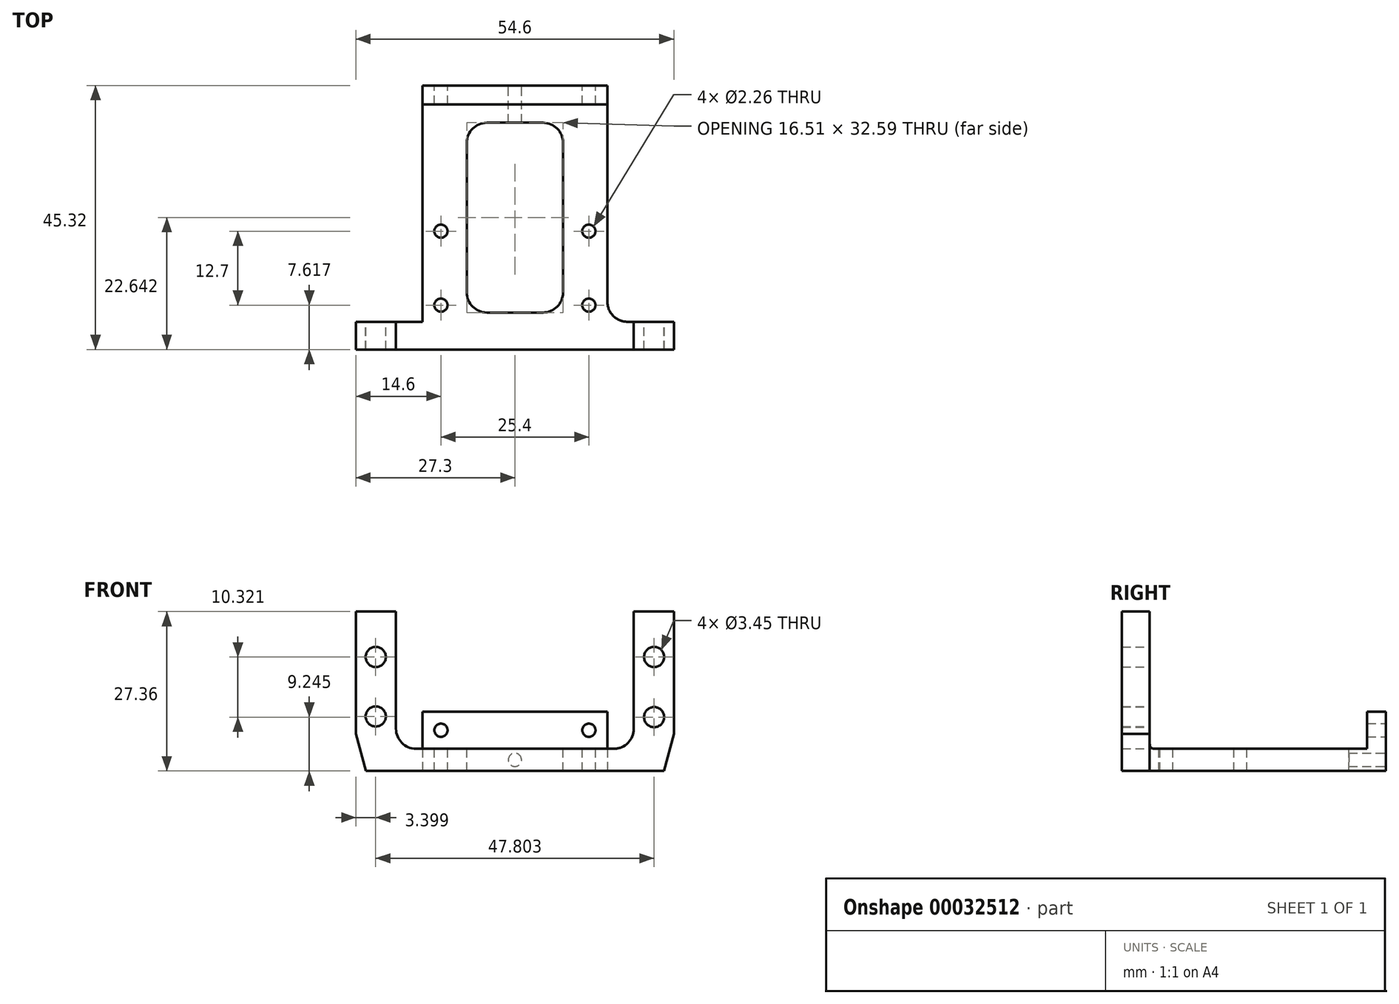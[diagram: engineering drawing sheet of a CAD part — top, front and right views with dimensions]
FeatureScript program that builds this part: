
annotation { "Feature Type Name" : "Feature", "Feature Type Description" : "" }
export const myFeature = defineFeature(function(context is Context, id is Id, definition is map)
    precondition{}
    {
        {
            var Q0;
            Q0=qCreatedBy(makeId("Front.planeOp"),FACE);
            var sketch = newSketch(context, id + "F0", { "sketchPlane" : qUnion([Q0])});
            skLineSegment(sketch, "E0.rect.bottom", {"start": v(0, -13.68) * mm, "end": v(-27.3, -13.68) * mm});
            skLineSegment(sketch, "E0.rect.right", {"start": v(-27.3, -7.33) * mm, "end": v(-27.3, 13.68) * mm});
            skPoint(sketch, "E0.rect.middle", {"position": v(0, 0) * mm});
            skLineSegment(sketch, "E1", {"start": v(0, -13.68) * mm, "end": v(0, 32.03) * mm, "construction": true});
            skPoint(sketch, "E1.endSnap0", {"position": v(0, 13.68) * mm});
            skLineSegment(sketch, "E2", {"start": v(-27.3, -13.68) * mm, "end": v(-55.76, -13.68) * mm, "construction": true});
            skLineSegment(sketch, "E3", {"start": v(-17, -9.87) * mm, "end": v(0, -9.87) * mm});
            skLineSegment(sketch, "E4", {"start": v(-20.42, 13.68) * mm, "end": v(-20.42, -6.44) * mm});
            skPoint(sketch, "E5.orphan", {"position": v(-27.3, -9.87) * mm});
            skPoint(sketch, "E6", {"position": v(-27.3, -7.33) * mm});
            skPoint(sketch, "E7", {"position": v(-25.6, -13.68) * mm});
            skLineSegment(sketch, "E8", {"start": v(-27.3, -7.33) * mm, "end": v(-25.6, -13.68) * mm});
            skLineSegment(sketch, "E9.trimOffspring", {"start": v(-20.42, 13.68) * mm, "end": v(-27.3, 13.68) * mm});
            skPoint(sketch, "E0.rect.left.end.orphan", {"position": v(27.3, 13.68) * mm});
            skPoint(sketch, "E10.orphan", {"position": v(27.3, -13.68) * mm});
            skLineSegment(sketch, "E11.MirrorCS", {"start": v(20.42, 13.68) * mm, "end": v(20.42, -6.44) * mm});
            skPoint(sketch, "E12.MirrorP", {"position": v(27.3, -9.87) * mm});
            skPoint(sketch, "E13.MirrorP", {"position": v(27.3, -7.33) * mm});
            skPoint(sketch, "E14.MirrorP", {"position": v(25.6, -13.68) * mm});
            skLineSegment(sketch, "E15.MirrorCS", {"start": v(27.3, -7.33) * mm, "end": v(25.6, -13.68) * mm});
            skLineSegment(sketch, "E16.MirrorCS", {"start": v(27.3, -7.33) * mm, "end": v(27.3, 13.68) * mm});
            skLineSegment(sketch, "E17.MirrorCS", {"start": v(20.42, 13.68) * mm, "end": v(27.3, 13.68) * mm});
            skLineSegment(sketch, "E18.MirrorCS", {"start": v(0, -13.68) * mm, "end": v(27.3, -13.68) * mm});
            skLineSegment(sketch, "E19.MirrorCS", {"start": v(17, -9.87) * mm, "end": v(0, -9.87) * mm});
            skPoint(sketch, "E20.visualSharp", {"position": v(-20.42, -9.87) * mm});
            skArc(sketch, "E20.filletArc", {"start": v(-20.42, -6.44) * mm, "mid": v(-19.42, -8.87) * mm, "end": v(-17, -9.87) * mm});
            skArc(sketch, "E21.MirrorCS", {"start": v(20.42, -6.44) * mm, "mid": v(19.42, -8.87) * mm, "end": v(17, -9.87) * mm});
            skPoint(sketch, "E22.orphan", {"position": v(20.42, -9.87) * mm});
            skSolve(sketch);
        }
        {
            var Q0;
            Q0=makeQuery(id+"F0.imprint","IMPRINT",FACE,{"disambiguationData":[TD([[makeQuery(id+"F0.imprint","IMPRINT",EDGE,{"derivedFrom":sQuery(id+"F0.wireOp",EDGE,"E0.rect.right")}),-1.0]])]});
            extrude(context, id + "F1", {"entities" : qUnion([Q0]), "depth" : 4.76 * mm});
        }
        {
            var Q0;
            Q0=makeQuery(id+"F1.opExtrude","CAP_FACE",FACE,{"disambiguationData":[OSD([sQuery(id+"F0.wireOp",EDGE,"E0.rect.bottom"),sQuery(id+"F0.wireOp",EDGE,"E0.rect.right"),sQuery(id+"F0.wireOp",EDGE,"E3"),sQuery(id+"F0.wireOp",EDGE,"E4"),sQuery(id+"F0.wireOp",EDGE,"E8"),sQuery(id+"F0.wireOp",EDGE,"E9.trimOffspring"),sQuery(id+"F0.wireOp",EDGE,"E11.MirrorCS"),sQuery(id+"F0.wireOp",EDGE,"E15.MirrorCS"),sQuery(id+"F0.wireOp",EDGE,"E16.MirrorCS"),sQuery(id+"F0.wireOp",EDGE,"E17.MirrorCS"),sQuery(id+"F0.wireOp",EDGE,"E18.MirrorCS"),sQuery(id+"F0.wireOp",EDGE,"E19.MirrorCS"),sQuery(id+"F0.wireOp",EDGE,"E20.filletArc"),sQuery(id+"F0.wireOp",EDGE,"E21.MirrorCS")])],"isStart":true});
            var sketch = newSketch(context, id + "F2", { "sketchPlane" : qUnion([Q0])});
            skLineSegment(sketch, "E23", {"start": v(0, -9.87) * mm, "end": v(-15.88, -9.87) * mm});
            skLineSegment(sketch, "E24", {"start": v(0, -9.87) * mm, "end": v(0, 6.26) * mm, "construction": true});
            skLineSegment(sketch, "E25", {"start": v(-24.83, -13.68) * mm, "end": v(-38.44, -13.68) * mm, "construction": true});
            skLineSegment(sketch, "E26", {"start": v(-15.88, -9.87) * mm, "end": v(-15.88, -13.68) * mm});
            skLineSegment(sketch, "E27", {"start": v(-15.88, -13.68) * mm, "end": v(0, -13.68) * mm});
            skLineSegment(sketch, "E28.MirrorCS", {"start": v(15.88, -9.87) * mm, "end": v(15.88, -13.68) * mm});
            skLineSegment(sketch, "E29.MirrorCS", {"start": v(15.88, -13.68) * mm, "end": v(0, -13.68) * mm});
            skLineSegment(sketch, "E30.MirrorCS", {"start": v(0, -9.87) * mm, "end": v(15.88, -9.87) * mm});
            skSolve(sketch);
        }
        {
            var Q0;
            Q0=makeQuery(id+"F2.imprint","IMPRINT",FACE,{"disambiguationData":[TD([[makeQuery(id+"F2.imprint","IMPRINT",EDGE,{"derivedFrom":sQuery(id+"F2.wireOp",EDGE,"E23")}),-1.0]])]});
            extrude(context, id + "F3", {"entities" : qUnion([Q0]), "operationType" : NewBodyOperationType.ADD, "depth" : 37.34 * mm});
        }
        {
            var Q0;
            Q0=makeQuery(id+"F3.opExtrude","CAP_EDGE",EDGE,{"disambiguationData":[OSD([sQuery(id+"F2.wireOp",EDGE,"E26")])],"isStart":true});
            var Q1;
            Q1=makeQuery(id+"F3.opExtrude","CAP_EDGE",EDGE,{"disambiguationData":[OSD([sQuery(id+"F2.wireOp",EDGE,"E28.MirrorCS")])],"isStart":true});
            fillet(context, id + "F4", {"entities" : qUnion([Q0, Q1]), "radius" : 3.43 * mm, "tangentPropagation" : true, "allowEdgeOverflow" : false});
        }
        {
            var Q0;
            Q0=makeQuery(id+"F3.opExtrude","CAP_FACE",FACE,{"disambiguationData":[OSD([sQuery(id+"F2.wireOp",EDGE,"E23"),sQuery(id+"F2.wireOp",EDGE,"E26"),sQuery(id+"F2.wireOp",EDGE,"E27"),sQuery(id+"F2.wireOp",EDGE,"E28.MirrorCS"),sQuery(id+"F2.wireOp",EDGE,"E29.MirrorCS"),sQuery(id+"F2.wireOp",EDGE,"E30.MirrorCS")])],"isStart":false});
            var sketch = newSketch(context, id + "F5", { "sketchPlane" : qUnion([Q0])});
            skLineSegment(sketch, "E31", {"start": v(-15.88, -13.68) * mm, "end": v(-15.88, -3.52) * mm});
            skLineSegment(sketch, "E32", {"start": v(15.88, -13.68) * mm, "end": v(15.88, -3.52) * mm});
            skPoint(sketch, "E32.endSnap0", {"position": v(15.88, -11.78) * mm});
            skLineSegment(sketch, "E33", {"start": v(-15.88, -3.52) * mm, "end": v(15.88, -3.52) * mm});
            skLineSegment(sketch, "E34", {"start": v(15.88, -13.68) * mm, "end": v(-15.88, -13.68) * mm});
            skSolve(sketch);
        }
        {
            var Q0;
            {var subQ1=sQuery(id+"F5.wireOp",EDGE,"E33");Q0=makeQuery(id+"F5.imprint","IMPRINT",FACE,{"disambiguationData":[TD([[makeQuery(id+"F5.imprint","IMPRINT",EDGE,{"derivedFrom":subQ1}),-1.0]])]});}
            var Q1;
            {var subQ1=sQuery(id+"F5.wireOp",EDGE,"E34");Q1=makeQuery(id+"F5.imprint","IMPRINT",FACE,{"disambiguationData":[TD([[makeQuery(id+"F5.imprint","IMPRINT",EDGE,{"derivedFrom":subQ1}),1.0]])]});}
            extrude(context, id + "F6", {"entities" : qUnion([Q0, Q1]), "operationType" : NewBodyOperationType.ADD, "depth" : 3.23 * mm});
        }
        {
            var Q0;
            Q0=qCreatedBy(makeId("Front.planeOp"),FACE);
            var sketch = newSketch(context, id + "F7", { "sketchPlane" : qUnion([Q0])});
            skLineSegment(sketch, "E35", {"start": v(0, -13.57) * mm, "end": v(0, 16.2) * mm, "construction": true});
            skLineSegment(sketch, "E36", {"start": v(0, -13.57) * mm, "end": v(-38.93, -13.57) * mm, "construction": true});
            skPoint(sketch, "E37", {"position": v(-23.9, -4.32) * mm});
            skPoint(sketch, "E38", {"position": v(-23.9, 5.89) * mm});
            skPoint(sketch, "E39", {"position": v(23.9, 5.89) * mm});
            skPoint(sketch, "E40", {"position": v(23.9, -4.43) * mm});
            skSolve(sketch);
        }
        {
            var Q0;
            Q0=sQuery(id+"F7.wireOp",VERTEX,"E38");
            var Q1;
            Q1=sQuery(id+"F7.wireOp",VERTEX,"E37");
            var Q2;
            Q2=sQuery(id+"F7.wireOp",VERTEX,"E40");
            var Q3;
            Q3=sQuery(id+"F7.wireOp",VERTEX,"E39");
            var Q4;
            Q4=makeQuery(id+"F1.opExtrude","SWEPT_BODY",BODY,{"disambiguationData":[OSD([sQuery(id+"F0.wireOp",EDGE,"E0.rect.bottom"),sQuery(id+"F0.wireOp",EDGE,"E0.rect.right"),sQuery(id+"F0.wireOp",EDGE,"E3"),sQuery(id+"F0.wireOp",EDGE,"E4"),sQuery(id+"F0.wireOp",EDGE,"E8"),sQuery(id+"F0.wireOp",EDGE,"E9.trimOffspring"),sQuery(id+"F0.wireOp",EDGE,"E11.MirrorCS"),sQuery(id+"F0.wireOp",EDGE,"E15.MirrorCS"),sQuery(id+"F0.wireOp",EDGE,"E16.MirrorCS"),sQuery(id+"F0.wireOp",EDGE,"E17.MirrorCS"),sQuery(id+"F0.wireOp",EDGE,"E18.MirrorCS"),sQuery(id+"F0.wireOp",EDGE,"E19.MirrorCS"),sQuery(id+"F0.wireOp",EDGE,"E20.filletArc"),sQuery(id+"F0.wireOp",EDGE,"E21.MirrorCS")])]});
            hole(context, id + "F8", {"style" : HoleStyle.SIMPLE, "holeDiameter" : 3.45 * mm, "endStyle" : HoleEndStyle.THROUGH, "oppositeDirection" : true, "locations" : qUnion([Q0, Q1, Q2, Q3]), "scope" : qUnion([Q4])});
        }
        {
            var Q0;
            Q0=makeQuery(id+"F6.opExtrude","CAP_FACE",FACE,{"disambiguationData":[OSD([sQuery(id+"F5.wireOp",EDGE,"E31"),sQuery(id+"F5.wireOp",EDGE,"E32"),sQuery(id+"F5.wireOp",EDGE,"E33"),sQuery(id+"F5.wireOp",EDGE,"E34")])],"isStart":false});
            var sketch = newSketch(context, id + "F9", { "sketchPlane" : qUnion([Q0])});
            skLineSegment(sketch, "E41", {"start": v(-15.88, -6.7) * mm, "end": v(15.88, -6.7) * mm});
            skLineSegment(sketch, "E42", {"start": v(0, -13.68) * mm, "end": v(0, 9.84) * mm, "construction": true});
            skPoint(sketch, "E42.endSnap0", {"position": v(0, -6.7) * mm});
            skLineSegment(sketch, "E43", {"start": v(0, -13.68) * mm, "end": v(-37.44, -13.68) * mm, "construction": true});
            skPoint(sketch, "E44", {"position": v(-12.7, -6.7) * mm});
            skPoint(sketch, "E45", {"position": v(12.7, -6.7) * mm});
            skPoint(sketch, "E46", {"position": v(0, -11.78) * mm});
            skSolve(sketch);
        }
        {
            var Q0;
            Q0=sQuery(id+"F9.wireOp",VERTEX,"E44");
            var Q1;
            Q1=sQuery(id+"F9.wireOp",VERTEX,"E45");
            var Q2;
            Q2=sQuery(id+"F9.wireOp",VERTEX,"E46");
            var Q3;
            Q3=makeQuery(id+"F1.opExtrude","SWEPT_BODY",BODY,{"disambiguationData":[OSD([sQuery(id+"F0.wireOp",EDGE,"E0.rect.bottom"),sQuery(id+"F0.wireOp",EDGE,"E0.rect.right"),sQuery(id+"F0.wireOp",EDGE,"E3"),sQuery(id+"F0.wireOp",EDGE,"E4"),sQuery(id+"F0.wireOp",EDGE,"E8"),sQuery(id+"F0.wireOp",EDGE,"E9.trimOffspring"),sQuery(id+"F0.wireOp",EDGE,"E11.MirrorCS"),sQuery(id+"F0.wireOp",EDGE,"E15.MirrorCS"),sQuery(id+"F0.wireOp",EDGE,"E16.MirrorCS"),sQuery(id+"F0.wireOp",EDGE,"E17.MirrorCS"),sQuery(id+"F0.wireOp",EDGE,"E18.MirrorCS"),sQuery(id+"F0.wireOp",EDGE,"E19.MirrorCS"),sQuery(id+"F0.wireOp",EDGE,"E20.filletArc"),sQuery(id+"F0.wireOp",EDGE,"E21.MirrorCS")])]});
            hole(context, id + "F10", {"style" : HoleStyle.SIMPLE, "holeDiameter" : 2.26 * mm, "endStyle" : HoleEndStyle.BLIND, "holeDepth" : 10.16 * mm, "locations" : qUnion([Q0, Q1, Q2]), "scope" : qUnion([Q3])});
        }
        {
            var Q0;
            Q0=makeQuery(id+"F3.boolean.opBoolean","MERGE",FACE,{"derivedFrom":[makeQuery(id+"F1.opExtrude","SWEPT_FACE",FACE,{"disambiguationData":[OSD([sQuery(id+"F0.wireOp",EDGE,"E3"),sQuery(id+"F0.wireOp",EDGE,"E19.MirrorCS")])]}),makeQuery(id+"F3.opExtrude","SWEPT_FACE",FACE,{"disambiguationData":[OSD([sQuery(id+"F2.wireOp",EDGE,"E23"),sQuery(id+"F2.wireOp",EDGE,"E30.MirrorCS")])]})]});
            var sketch = newSketch(context, id + "F11", { "sketchPlane" : qUnion([Q0])});
            skLineSegment(sketch, "E47.bottom", {"start": v(4.83, 1.59) * mm, "end": v(-4.83, 1.59) * mm});
            skLineSegment(sketch, "E47.top", {"start": v(4.83, 34.18) * mm, "end": v(-4.83, 34.18) * mm});
            skLineSegment(sketch, "E47.left", {"start": v(8.26, 5.02) * mm, "end": v(8.26, 30.75) * mm});
            skLineSegment(sketch, "E47.right", {"start": v(-8.26, 5.02) * mm, "end": v(-8.26, 30.75) * mm});
            skLineSegment(sketch, "E48", {"start": v(0, 0) * mm, "end": v(0, 47.79) * mm, "construction": true});
            skLineSegment(sketch, "E49", {"start": v(0, -4.76) * mm, "end": v(-43.2, -4.76) * mm, "construction": true});
            skPoint(sketch, "E50.visualSharp", {"position": v(8.26, 1.59) * mm});
            skArc(sketch, "E50.filletArc", {"start": v(4.83, 1.59) * mm, "mid": v(7.25, 2.6) * mm, "end": v(8.26, 5.02) * mm});
            skPoint(sketch, "E51.visualSharp", {"position": v(-8.26, 1.59) * mm});
            skArc(sketch, "E51.filletArc", {"start": v(-8.26, 5.02) * mm, "mid": v(-7.25, 2.6) * mm, "end": v(-4.83, 1.59) * mm});
            skPoint(sketch, "E52.visualSharp", {"position": v(-8.26, 34.18) * mm});
            skArc(sketch, "E52.filletArc", {"start": v(-4.83, 34.18) * mm, "mid": v(-7.25, 33.17) * mm, "end": v(-8.26, 30.75) * mm});
            skPoint(sketch, "E53.visualSharp", {"position": v(8.26, 34.18) * mm});
            skArc(sketch, "E53.filletArc", {"start": v(8.26, 30.75) * mm, "mid": v(7.25, 33.17) * mm, "end": v(4.83, 34.18) * mm});
            skSolve(sketch);
        }
        {
            var Q0;
            Q0=makeQuery(id+"F11.imprint","IMPRINT",FACE,{"disambiguationData":[TD([[makeQuery(id+"F11.imprint","IMPRINT",EDGE,{"derivedFrom":sQuery(id+"F11.wireOp",EDGE,"E47.bottom")}),-1.0]])]});
            extrude(context, id + "F12", {"entities" : qUnion([Q0]), "operationType" : NewBodyOperationType.REMOVE, "endBound" : BoundingType.THROUGH_ALL, "oppositeDirection" : true, "depth" : 25.4 * mm});
        }
        {
            var Q0;
            Q0=makeQuery(id+"F3.boolean.opBoolean","MERGE",FACE,{"derivedFrom":[makeQuery(id+"F1.opExtrude","SWEPT_FACE",FACE,{"disambiguationData":[OSD([sQuery(id+"F0.wireOp",EDGE,"E3"),sQuery(id+"F0.wireOp",EDGE,"E19.MirrorCS")])]}),makeQuery(id+"F3.opExtrude","SWEPT_FACE",FACE,{"disambiguationData":[OSD([sQuery(id+"F2.wireOp",EDGE,"E23"),sQuery(id+"F2.wireOp",EDGE,"E30.MirrorCS")])]})]});
            var sketch = newSketch(context, id + "F13", { "sketchPlane" : qUnion([Q0])});
            skLineSegment(sketch, "E54", {"start": v(0, -4.76) * mm, "end": v(0, 32.22) * mm, "construction": true});
            skLineSegment(sketch, "E55", {"start": v(-9.11, -4.76) * mm, "end": v(-39.22, -4.76) * mm, "construction": true});
            skPoint(sketch, "E56", {"position": v(12.7, 2.86) * mm});
            skPoint(sketch, "E57", {"position": v(12.7, 15.56) * mm});
            skPoint(sketch, "E58.MirrorP", {"position": v(-12.7, 2.86) * mm});
            skPoint(sketch, "E59.MirrorP", {"position": v(-12.7, 15.56) * mm});
            skSolve(sketch);
        }
        {
            var Q0;
            Q0=sQuery(id+"F13.wireOp",VERTEX,"E56");
            var Q1;
            Q1=sQuery(id+"F13.wireOp",VERTEX,"E57");
            var Q2;
            Q2=sQuery(id+"F13.wireOp",VERTEX,"E58.MirrorP");
            var Q3;
            Q3=sQuery(id+"F13.wireOp",VERTEX,"E59.MirrorP");
            var Q4;
            Q4=makeQuery(id+"F1.opExtrude","SWEPT_BODY",BODY,{"disambiguationData":[OSD([sQuery(id+"F0.wireOp",EDGE,"E0.rect.bottom"),sQuery(id+"F0.wireOp",EDGE,"E0.rect.right"),sQuery(id+"F0.wireOp",EDGE,"E3"),sQuery(id+"F0.wireOp",EDGE,"E4"),sQuery(id+"F0.wireOp",EDGE,"E8"),sQuery(id+"F0.wireOp",EDGE,"E9.trimOffspring"),sQuery(id+"F0.wireOp",EDGE,"E11.MirrorCS"),sQuery(id+"F0.wireOp",EDGE,"E15.MirrorCS"),sQuery(id+"F0.wireOp",EDGE,"E16.MirrorCS"),sQuery(id+"F0.wireOp",EDGE,"E17.MirrorCS"),sQuery(id+"F0.wireOp",EDGE,"E18.MirrorCS"),sQuery(id+"F0.wireOp",EDGE,"E19.MirrorCS"),sQuery(id+"F0.wireOp",EDGE,"E20.filletArc"),sQuery(id+"F0.wireOp",EDGE,"E21.MirrorCS")])]});
            hole(context, id + "F14", {"style" : HoleStyle.SIMPLE, "holeDiameter" : 2.26 * mm, "endStyle" : HoleEndStyle.THROUGH, "locations" : qUnion([Q0, Q1, Q2, Q3]), "scope" : qUnion([Q4])});
        }
    });
